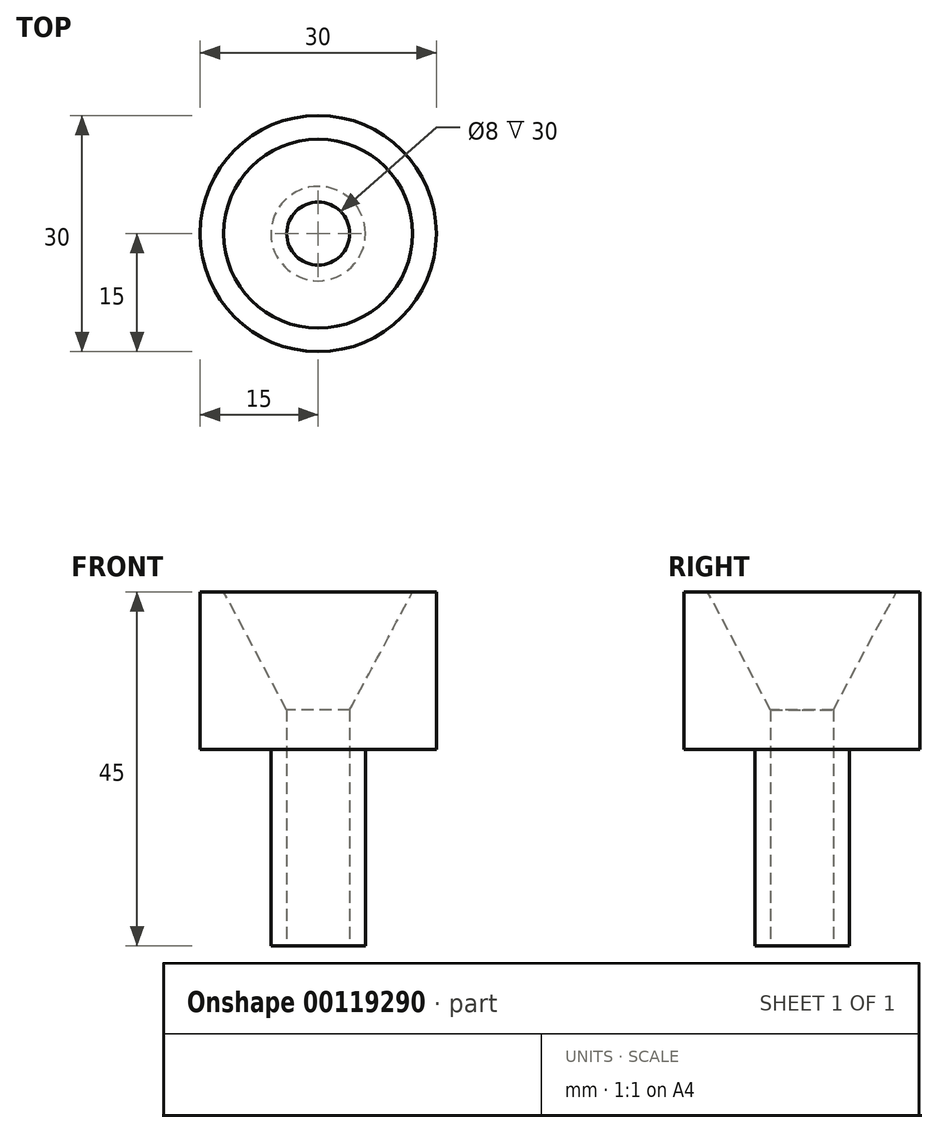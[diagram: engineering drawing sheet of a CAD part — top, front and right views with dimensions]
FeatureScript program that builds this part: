
annotation { "Feature Type Name" : "Feature", "Feature Type Description" : "" }
export const myFeature = defineFeature(function(context is Context, id is Id, definition is map)
    precondition{}
    {
        {
            var Q0;
            Q0=qCreatedBy(makeId("Top.planeOp"),FACE);
            var sketch = newSketch(context, id + "F0", { "sketchPlane" : qUnion([Q0])});
            skCircle(sketch, "E0", {"center": v(0, 0) * mm, "radius": 15 * mm});
            skCircle(sketch, "E1", {"center": v(0, 0) * mm, "radius": 4 * mm});
            skSolve(sketch);
        }
        {
            var Q0;
            Q0 = qSketchRegion(id + "F0", true);
            extrude(context, id + "F1", {"entities" : qUnion([Q0]), "depth" : 20 * mm});
        }
        {
            var Q0;
            Q0=makeQuery(id+"F1.opExtrude","CAP_EDGE",EDGE,{"disambiguationData":[OSD([sQuery(id+"F0.wireOp",EDGE,"E1")])],"isStart":false});
            chamfer(context, id + "F2", {"entities" : qUnion([Q0]), "chamferType" : ChamferType.TWO_OFFSETS, "width1" : 15 * mm, "oppositeDirection" : false, "width2" : 8 * mm, "tangentPropagation" : true});
        }
        {
            var Q0;
            Q0=makeQuery(id+"F1.opExtrude","CAP_FACE",FACE,{"disambiguationData":[OSD([sQuery(id+"F0.wireOp",EDGE,"E0"),sQuery(id+"F0.wireOp",EDGE,"E1")])],"isStart":true});
            var sketch = newSketch(context, id + "F3", { "sketchPlane" : qUnion([Q0])});
            skCircle(sketch, "E2", {"center": v(0, 0) * mm, "radius": 6 * mm});
            skCircle(sketch, "E3", {"center": v(0, 0) * mm, "radius": 4 * mm});
            skSolve(sketch);
        }
        {
            var Q0;
            Q0 = qSketchRegion(id + "F3", true);
            extrude(context, id + "F4", {"entities" : qUnion([Q0]), "operationType" : NewBodyOperationType.ADD, "depth" : 25 * mm});
        }
    });
